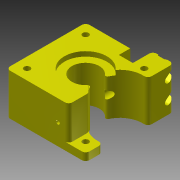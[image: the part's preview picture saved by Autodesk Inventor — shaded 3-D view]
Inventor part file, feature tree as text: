
AUTODESK INVENTOR PART (.ipt)
format: ipt  version: 2013 (Build 170138000, 138)  size: 377,856 bytes
history: native  units: mm
features: extrude x18, sketch x18, projected_geometry x5, fillet x4
ambient origin geometry x8: Origin, YZ Plane, XZ Plane, XY Plane, X Axis, Y Axis, Z Axis, Center Point
bodies: Solid1 (feature_tree)
feature tree (45):
  extrude  "Extrusion1"  Depth=22.0mm TaperAngle=0.0deg
  extrude  "Extrusion2"  Depth=20.0mm TaperAngle=0.0deg
  extrude  "Extrusion3"  Depth=1.75mm
  extrude  "Extrusion4"  Depth=24.0mm
  extrude  "Extrusion5"  Depth=10.795mm
  extrude  "Extrusion6"  Depth=2.0mm
  extrude  "Extrusion7"  Depth=4.2mm
  extrude  "Extrusion10"  Depth=31.0mm
  extrude  "Extrusion11"  Depth=20.0mm TaperAngle=0.0deg
  extrude  "Extrusion12"  Depth=2.5mm TaperAngle=0.0deg
  extrude  "Extrusion20"  Depth=7.4mm
  extrude  "Extrusion21"  Depth=5.5mm
  extrude  "Extrusion22"  Depth=3.5mm TaperAngle=0.0deg
  extrude  "Extrusion23"  Depth=12.0mm
  fillet  "Fillet5"  Radius=3.2mm
  fillet  "Fillet6"  Radius=7.1mm
  extrude  "Extrusion16"  Depth=6.0mm
  extrude  "Extrusion17"  Depth=3.0mm TaperAngle=0.0deg
  extrude  "Extrusion18"  Depth=14.0mm
  extrude  "Extrusion19"  Depth=10.0mm
  fillet  "Fillet4"  Radius=1.6mm
  fillet  "Fillet3"  Radius=3.0mm
  sketch  "Sketch1"  dims[d0=42.0mm d2=22.0mm d3=0.0mm]
  sketch  "Sketch3"  dims[d4=14.5mm d7=20.0mm d8=0.0mm]
  sketch  "Sketch4"  dims[d9=10.795mm d11=1.75mm]
  sketch  "Sketch5"  dims[d12=22.0mm d14=24.0mm]
  sketch  "Sketch6"  dims[d15=14.5mm d16=0.0mm d18=10.795mm]
  sketch  "Sketch7"  dims[d20=1.75mm d21=2.0mm]
  sketch  "Sketch8"  dims[d22=20.0mm d23=0.0mm d24=4.2mm]
  sketch  "Sketch11"  dims[d26=20.0mm d27=0.0mm d28=31.0mm]
  sketch  "Sketch12"  dims[d29=3.2mm d30=20.0mm d31=0.0mm]
  sketch  "Sketch13"  dims[d32=22.5mm d34=2.5mm d35=0.0mm]
  sketch  "Sketch18"  dims[d42=2.5mm d43=0.0mm d44=7.4mm]
  sketch  "Sketch19"  dims[d45=3.5mm d46=0.0mm d47=5.5mm]
  sketch  "Sketch20"  dims[d48=7.4mm d49=3.5mm d50=0.0mm]
  projected_geometry  "Projected Loop1"
  sketch  "Sketch21"  dims[d62=4.0mm d63=12.0mm d64=3.2mm d65=7.1mm d66=0.0mm]
  projected_geometry  "Projected Loop2"
  sketch  "Sketch22"  dims[d67=7.1mm d68=0.0mm d69=6.0mm]
  sketch  "Sketch23"  dims[d71=3.0mm d72=0.0mm d73=3.0mm d74=0.0mm]
  sketch  "Sketch24"  dims[d75=4.0mm d76=14.0mm]
  projected_geometry  "Projected Loop3"
  projected_geometry  "Projected Loop4"
  sketch  "Sketch25"  dims[d78=9.0mm d79=0.0mm d80=10.0mm d82=1.6mm d83=3.0mm d84=22.68928mm d85=5.0mm d86=0.0mm d87=3.0mm d88=0.0mm d89=3.0mm d91=3.0mm d92=0.0mm d93=2.0mm d94=1.0mm]
  projected_geometry  "Projected Loop5"
